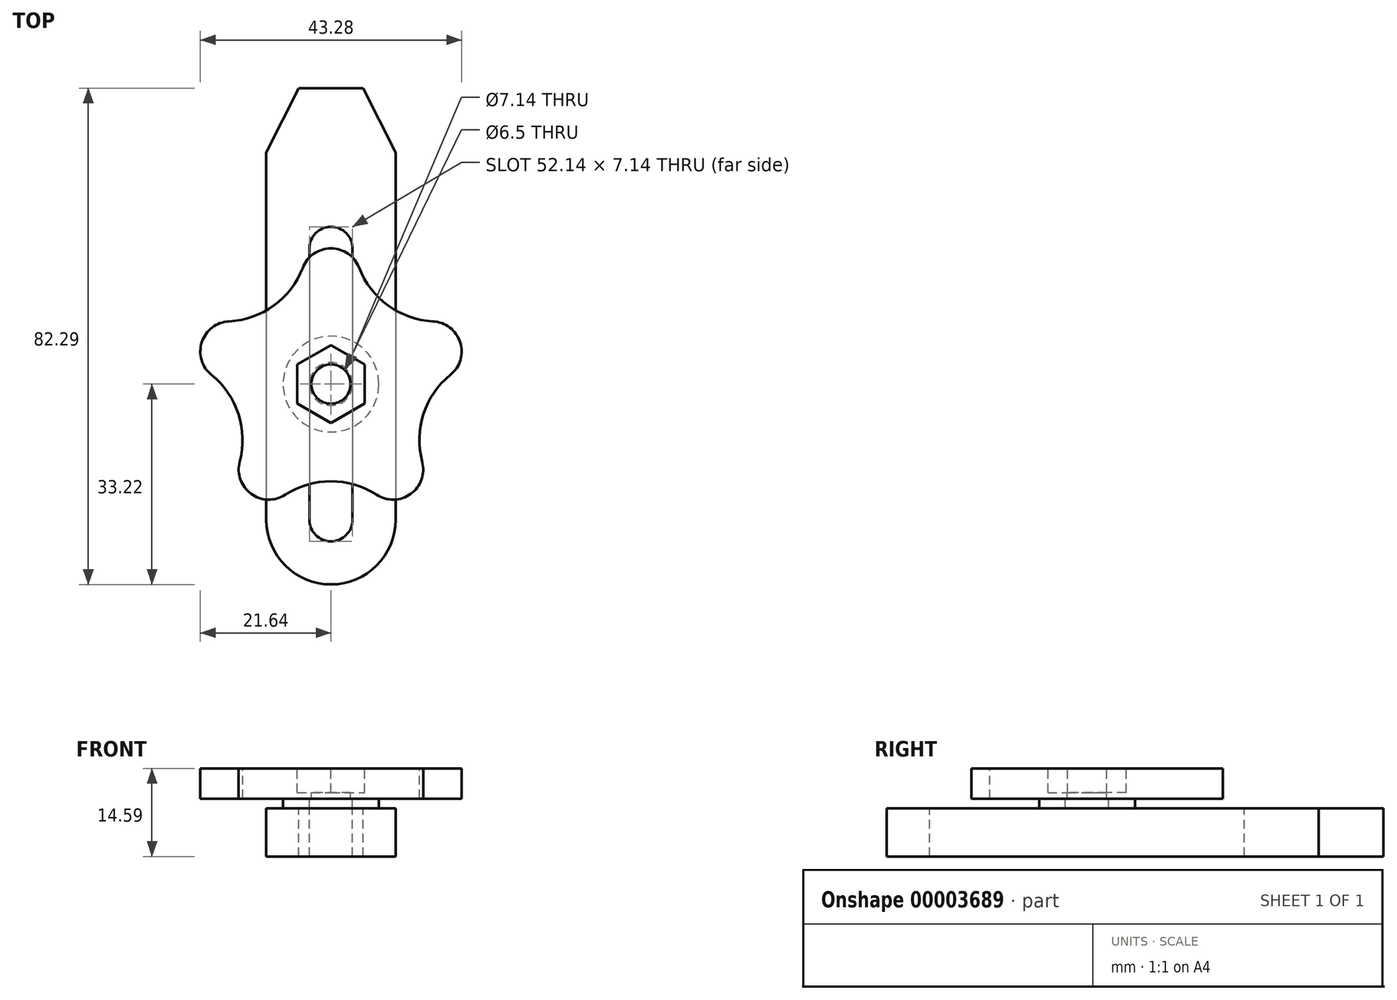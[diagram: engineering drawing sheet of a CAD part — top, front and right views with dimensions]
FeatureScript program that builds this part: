
annotation { "Feature Type Name" : "Feature", "Feature Type Description" : "" }
export const myFeature = defineFeature(function(context is Context, id is Id, definition is map)
    precondition{}
    {
        {
            var Q0;
            Q0=qCreatedBy(makeId("Top.planeOp"),FACE);
            var sketch = newSketch(context, id + "F0", { "sketchPlane" : qUnion([Q0])});
            skCircle(sketch, "E0.cCircle", {"center": v(0, 0) * mm, "radius": 14.16 * mm, "construction": true});
            skLineSegment(sketch, "E0.0", {"start": v(0, 17.5) * mm, "end": v(16.64, 5.4) * mm, "construction": true});
            skLineSegment(sketch, "E0.1", {"start": v(16.64, 5.4) * mm, "end": v(10.29, -14.16) * mm, "construction": true});
            skLineSegment(sketch, "E0.2", {"start": v(10.29, -14.16) * mm, "end": v(-10.29, -14.16) * mm, "construction": true});
            skLineSegment(sketch, "E0.3", {"start": v(-10.29, -14.16) * mm, "end": v(-16.64, 5.4) * mm, "construction": true});
            skLineSegment(sketch, "E0.4", {"start": v(-16.64, 5.4) * mm, "end": v(0, 17.5) * mm, "construction": true});
            skPoint(sketch, "E0.0.midPoint", {"position": v(8.32, 11.45) * mm});
            skCircle(sketch, "E1", {"center": v(0, 17.5) * mm, "radius": 5 * mm});
            skCircle(sketch, "E2", {"center": v(16.64, 5.4) * mm, "radius": 5 * mm});
            skCircle(sketch, "E3", {"center": v(10.29, -14.16) * mm, "radius": 5 * mm});
            skCircle(sketch, "E4", {"center": v(-10.29, -14.16) * mm, "radius": 5 * mm});
            skCircle(sketch, "E5", {"center": v(-16.64, 5.4) * mm, "radius": 5 * mm});
            skLineSegment(sketch, "E6", {"start": v(-10.29, -19.16) * mm, "end": v(10.29, -19.16) * mm, "construction": true});
            skArc(sketch, "E7", {"start": v(-16.9, 10.4) * mm, "mid": v(-9.47, 13.03) * mm, "end": v(-4.67, 19.3) * mm});
            skArc(sketch, "E8", {"start": v(4.67, 19.3) * mm, "mid": v(9.47, 13.03) * mm, "end": v(16.9, 10.4) * mm});
            skArc(sketch, "E9", {"start": v(19.8, 1.52) * mm, "mid": v(15.32, -4.98) * mm, "end": v(15.12, -12.86) * mm});
            skArc(sketch, "E10", {"start": v(7.56, -18.35) * mm, "mid": v(0, -16.11) * mm, "end": v(-7.56, -18.35) * mm});
            skArc(sketch, "E11", {"start": v(-15.12, -12.86) * mm, "mid": v(-15.32, -4.98) * mm, "end": v(-19.8, 1.52) * mm});
            skCircle(sketch, "E12", {"center": v(0, 0) * mm, "radius": 30 * mm, "construction": true});
            skCircle(sketch, "E13", {"center": v(0, 0) * mm, "radius": 22.5 * mm, "construction": true});
            skCircle(sketch, "E14.cCircle", {"center": v(0, 0) * mm, "radius": 5.6 * mm, "construction": true});
            skLineSegment(sketch, "E14.0", {"start": v(0, 6.47) * mm, "end": v(5.6, 3.23) * mm});
            skLineSegment(sketch, "E14.1", {"start": v(5.6, 3.23) * mm, "end": v(5.6, -3.23) * mm});
            skLineSegment(sketch, "E14.2", {"start": v(5.6, -3.23) * mm, "end": v(0, -6.47) * mm});
            skLineSegment(sketch, "E14.3", {"start": v(0, -6.47) * mm, "end": v(-5.6, -3.23) * mm});
            skLineSegment(sketch, "E14.4", {"start": v(-5.6, -3.23) * mm, "end": v(-5.6, 3.23) * mm});
            skLineSegment(sketch, "E14.5", {"start": v(-5.6, 3.23) * mm, "end": v(0, 6.47) * mm});
            skPoint(sketch, "E14.0.midPoint", {"position": v(2.8, 4.85) * mm});
            skCircle(sketch, "E15", {"center": v(0, 0) * mm, "radius": 3.25 * mm});
            skSolve(sketch);
        }
        {
            var Q0;
            Q0=qSketchRegion(id+"F0",true);
            var Q1;
            Q1=makeQuery(id+"F0.imprint","IMPRINT",FACE,{"disambiguationData":[TD([[makeQuery(id+"F0.imprint","IMPRINT",EDGE,{"derivedFrom":sQuery(id+"F0.wireOp",EDGE,"E14.0")}),-1.0]])]});
            extrude(context, id + "F1", {"entities" : qUnion([Q0, Q1]), "oppositeDirection" : true, "depth" : 5 * mm});
        }
        {
            var Q0;
            Q0=makeQuery(id+"F0.imprint","IMPRINT",FACE,{"disambiguationData":[TD([[makeQuery(id+"F0.imprint","IMPRINT",EDGE,{"derivedFrom":sQuery(id+"F0.wireOp",EDGE,"E14.0")}),-1.0]])]});
            extrude(context, id + "F2", {"entities" : qUnion([Q0]), "operationType" : NewBodyOperationType.REMOVE, "oppositeDirection" : true, "depth" : 4 * mm});
        }
        {
            var Q0;
            Q0=makeQuery(id+"F1.opExtrude","CAP_FACE",FACE,{"disambiguationData":[OSD([sQuery(id+"F0.wireOp",EDGE,"E1"),sQuery(id+"F0.wireOp",EDGE,"E2"),sQuery(id+"F0.wireOp",EDGE,"E3"),sQuery(id+"F0.wireOp",EDGE,"E4"),sQuery(id+"F0.wireOp",EDGE,"E5"),sQuery(id+"F0.wireOp",EDGE,"E7"),sQuery(id+"F0.wireOp",EDGE,"E8"),sQuery(id+"F0.wireOp",EDGE,"E9"),sQuery(id+"F0.wireOp",EDGE,"E10"),sQuery(id+"F0.wireOp",EDGE,"E11"),sQuery(id+"F0.wireOp",EDGE,"E15")])],"isStart":false});
            var sketch = newSketch(context, id + "F3", { "sketchPlane" : qUnion([Q0])});
            skCircle(sketch, "E16", {"center": v(0, 0) * mm, "radius": 7.94 * mm});
            skCircle(sketch, "E17", {"center": v(0, 0) * mm, "radius": 3.57 * mm});
            skSolve(sketch);
        }
        {
            var Q0;
            Q0=makeQuery(id+"F3.imprint","IMPRINT",FACE,{"disambiguationData":[TD([[makeQuery(id+"F3.imprint","IMPRINT",EDGE,{"derivedFrom":sQuery(id+"F3.wireOp",EDGE,"E16")}),1.0]])]});
            extrude(context, id + "F4", {"entities" : qUnion([Q0]), "depth" : (1 / 16 * 25.4) * mm});
        }
        {
            var Q0;
            Q0=makeQuery(id+"F4.opExtrude","CAP_FACE",FACE,{"disambiguationData":[OSD([sQuery(id+"F3.wireOp",EDGE,"E16"),sQuery(id+"F3.wireOp",EDGE,"E17")])],"isStart":false});
            var sketch = newSketch(context, id + "F5", { "sketchPlane" : qUnion([Q0])});
            skLineSegment(sketch, "E18.rect.bottom", {"start": v(3.57, -22.5) * mm, "end": v(-3.57, -22.5) * mm});
            skLineSegment(sketch, "E18.rect.top", {"start": v(3.57, 22.5) * mm, "end": v(-3.57, 22.5) * mm});
            skLineSegment(sketch, "E18.rect.left", {"start": v(3.57, -22.5) * mm, "end": v(3.57, 22.5) * mm});
            skLineSegment(sketch, "E18.rect.right", {"start": v(-3.57, -22.5) * mm, "end": v(-3.57, 22.5) * mm});
            skPoint(sketch, "E18.rect.middle", {"position": v(0, 0) * mm});
            skLineSegment(sketch, "E19.bottom", {"start": v(-10.72, -38.36) * mm, "end": v(10.72, -38.36) * mm});
            skLineSegment(sketch, "E19.top", {"start": v(-10.72, 22.5) * mm, "end": v(10.72, 22.5) * mm});
            skLineSegment(sketch, "E19.left", {"start": v(-10.72, -38.36) * mm, "end": v(-10.72, 22.5) * mm});
            skLineSegment(sketch, "E19.right", {"start": v(10.72, -38.36) * mm, "end": v(10.72, 22.5) * mm});
            skArc(sketch, "E20", {"start": v(-3.57, -22.5) * mm, "mid": v(0, -26.07) * mm, "end": v(3.57, -22.5) * mm});
            skArc(sketch, "E21", {"start": v(3.57, 22.5) * mm, "mid": v(0, 26.07) * mm, "end": v(-3.57, 22.5) * mm});
            skLineSegment(sketch, "E22", {"start": v(-10.72, -38.36) * mm, "end": v(-5.36, -49.07) * mm});
            skLineSegment(sketch, "E23", {"start": v(-5.36, -49.07) * mm, "end": v(5.36, -49.07) * mm});
            skLineSegment(sketch, "E24", {"start": v(5.36, -49.07) * mm, "end": v(10.72, -38.36) * mm});
            skPoint(sketch, "E25", {"position": v(0, -49.07) * mm});
            skLineSegment(sketch, "E26", {"start": v(-10.72, -38.36) * mm, "end": v(0, -38.36) * mm, "construction": true});
            skLineSegment(sketch, "E27", {"start": v(0, -38.36) * mm, "end": v(0, -49.07) * mm, "construction": true});
            skArc(sketch, "E28", {"start": v(10.72, 22.5) * mm, "mid": v(0, 33.22) * mm, "end": v(-10.72, 22.5) * mm});
            skLineSegment(sketch, "E29", {"start": v(3.57, 0) * mm, "end": v(10.72, 0) * mm, "construction": true});
            skLineSegment(sketch, "E30", {"start": v(-3.57, 0) * mm, "end": v(-10.72, 0) * mm, "construction": true});
            skLineSegment(sketch, "E31", {"start": v(3.57, 0) * mm, "end": v(-3.57, 0) * mm, "construction": true});
            skSolve(sketch);
        }
        {
            var Q0;
            Q0=makeQuery(id+"F5.imprint","IMPRINT",FACE,{"disambiguationData":[TD([[makeQuery(id+"F5.imprint","IMPRINT",EDGE,{"derivedFrom":sQuery(id+"F5.wireOp",EDGE,"E19.bottom")}),-1.0]])]});
            var Q1;
            Q1=makeQuery(id+"F5.imprint","IMPRINT",FACE,{"disambiguationData":[TD([[makeQuery(id+"F5.imprint","IMPRINT",EDGE,{"derivedFrom":sQuery(id+"F5.wireOp",EDGE,"E19.top")}),1.0]])]});
            var Q2;
            {var subQ0=makeQuery(id+"F4.opExtrude","CAP_EDGE",EDGE,{"disambiguationData":[OSD([sQuery(id+"F3.wireOp",EDGE,"E16")])],"isStart":false});var subQ1=sQuery(id+"F5.wireOp",EDGE,"E18.rect.left");var subQ4=makeQuery(id+"F5.imprint","INTERSECT",VERTEX,{"disambiguationData":[OD(0.0)],"derivedFrom":[subQ0,subQ1]});Q2=makeQuery(id+"F5.imprint","IMPRINT",FACE,{"disambiguationData":[TD([[makeQuery(id+"F5.imprint","IMPRINT",EDGE,{"disambiguationData":[TD([[subQ4,-1.0]])],"derivedFrom":subQ1}),-1.0]])]});}
            var Q3;
            {var subQ0=makeQuery(id+"F4.opExtrude","CAP_EDGE",EDGE,{"disambiguationData":[OSD([sQuery(id+"F3.wireOp",EDGE,"E16")])],"isStart":false});var subQ1=sQuery(id+"F5.wireOp",EDGE,"E18.rect.right");var subQ4=makeQuery(id+"F5.imprint","INTERSECT",VERTEX,{"disambiguationData":[OD(0.0)],"derivedFrom":[subQ0,subQ1]});Q3=makeQuery(id+"F5.imprint","IMPRINT",FACE,{"disambiguationData":[TD([[makeQuery(id+"F5.imprint","IMPRINT",EDGE,{"disambiguationData":[TD([[subQ4,-1.0]])],"derivedFrom":subQ1}),1.0]])]});}
            var Q4;
            {var subQ10=sQuery(id+"F5.wireOp",EDGE,"E19.bottom");Q4=makeQuery(id+"F5.imprint","IMPRINT",FACE,{"disambiguationData":[TD([[makeQuery(id+"F5.imprint","IMPRINT",EDGE,{"derivedFrom":subQ10}),1.0]])]});}
            extrude(context, id + "F6", {"entities" : qUnion([Q0, Q1, Q2, Q3, Q4]), "depth" : 8 * mm});
        }
    });
